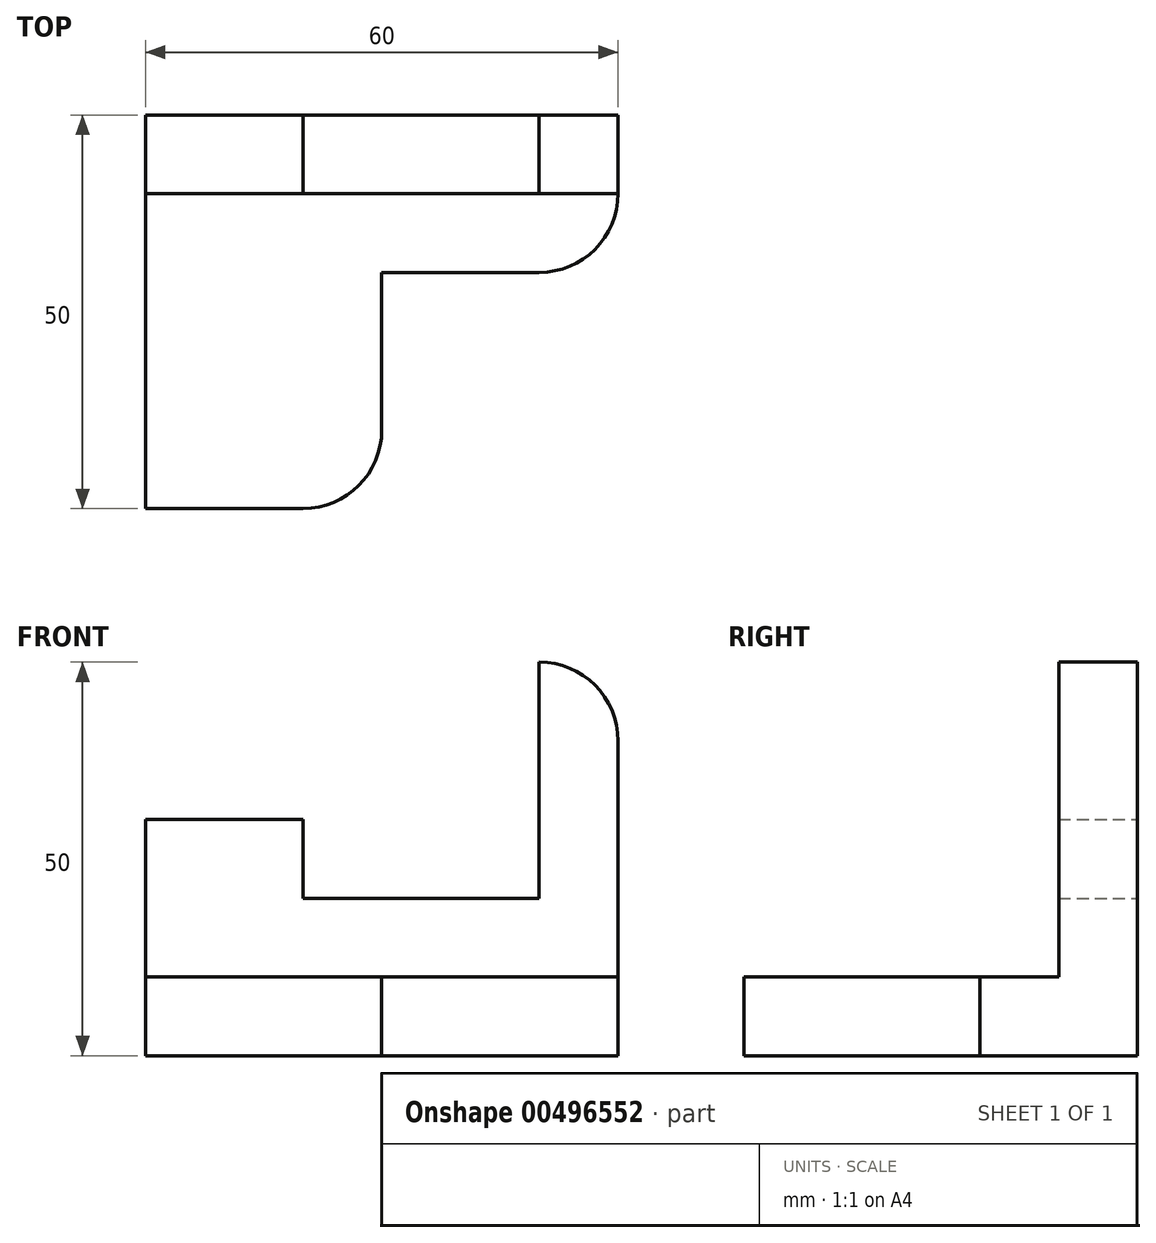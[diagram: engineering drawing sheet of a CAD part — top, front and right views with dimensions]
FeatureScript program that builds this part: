
annotation { "Feature Type Name" : "Feature", "Feature Type Description" : "" }
export const myFeature = defineFeature(function(context is Context, id is Id, definition is map)
    precondition{}
    {
        {
            var Q0;
            Q0=qCreatedBy(makeId("Top.planeOp"),FACE);
            var sketch = newSketch(context, id + "F0", { "sketchPlane" : qUnion([Q0])});
            skLineSegment(sketch, "E0", {"start": v(20, 0) * mm, "end": v(0, 0) * mm});
            skPoint(sketch, "E1.visualSharp", {"position": v(60, 30) * mm});
            skPoint(sketch, "E2.visualSharp", {"position": v(30, 0) * mm});
            skLineSegment(sketch, "E3", {"start": v(0, 0) * mm, "end": v(60, 0) * mm});
            skLineSegment(sketch, "E4", {"start": v(60, 0) * mm, "end": v(60, -10) * mm});
            skLineSegment(sketch, "E5", {"start": v(50, -20) * mm, "end": v(30, -20) * mm});
            skLineSegment(sketch, "E6", {"start": v(0, 0) * mm, "end": v(0, -50) * mm});
            skLineSegment(sketch, "E7", {"start": v(0, -50) * mm, "end": v(20, -50) * mm});
            skLineSegment(sketch, "E8", {"start": v(30, -40) * mm, "end": v(30, -20) * mm});
            skPoint(sketch, "E9.end.orphan", {"position": v(30, 30) * mm});
            skPoint(sketch, "E10.start.orphan", {"position": v(60, 50) * mm});
            skPoint(sketch, "E11.visualSharp", {"position": v(60, -20) * mm});
            skArc(sketch, "E11.filletArc", {"start": v(50, -20) * mm, "mid": v(57.07, -17.07) * mm, "end": v(60, -10) * mm});
            skPoint(sketch, "E12.visualSharp", {"position": v(30, -50) * mm});
            skArc(sketch, "E12.filletArc", {"start": v(20, -50) * mm, "mid": v(27.07, -47.07) * mm, "end": v(30, -40) * mm});
            skSolve(sketch);
        }
        {
            var Q0;
            Q0=makeQuery(id+"F0.imprint","IMPRINT",FACE,{"disambiguationData":[TD([[makeQuery(id+"F0.imprint","IMPRINT",EDGE,{"derivedFrom":sQuery(id+"F0.wireOp",EDGE,"GN2Li1Eq-WtNi-iwNF-XVSt-34LqWLU6xrt7")}),-1.0]])]});
            var Q1;
            {var subQ1=sQuery(id+"F0.wireOp",EDGE,"E4");Q1=makeQuery(id+"F0.imprint","IMPRINT",FACE,{"disambiguationData":[TD([[makeQuery(id+"F0.imprint","IMPRINT",EDGE,{"derivedFrom":subQ1}),-1.0]])]});}
            extrude(context, id + "F1", {"entities" : qUnion([Q0, Q1]), "depth" : 10 * mm});
        }
        {
            var Q0;
            Q0=qCreatedBy(makeId("Front.planeOp"),FACE);
            var sketch = newSketch(context, id + "F2", { "sketchPlane" : qUnion([Q0])});
            skLineSegment(sketch, "E13", {"start": v(0, 0) * mm, "end": v(0, 30) * mm});
            skLineSegment(sketch, "E14", {"start": v(0, 30) * mm, "end": v(20, 30) * mm});
            skLineSegment(sketch, "E15", {"start": v(20, 30) * mm, "end": v(20, 20) * mm});
            skLineSegment(sketch, "E16", {"start": v(20, 20) * mm, "end": v(50, 20) * mm});
            skLineSegment(sketch, "E17", {"start": v(50, 20) * mm, "end": v(50, 50) * mm});
            skLineSegment(sketch, "E18", {"start": v(50, 50) * mm, "end": v(50, 50) * mm});
            skLineSegment(sketch, "E19", {"start": v(60, 40) * mm, "end": v(60, 10) * mm});
            skLineSegment(sketch, "E20", {"start": v(60, 10) * mm, "end": v(0, 10) * mm});
            skPoint(sketch, "E21.visualSharp", {"position": v(60, 50) * mm});
            skArc(sketch, "E21.filletArc", {"start": v(60, 40) * mm, "mid": v(57.07, 47.07) * mm, "end": v(50, 50) * mm});
            skSolve(sketch);
        }
        {
            var Q0;
            Q0 = qSketchRegion(id + "F2", true);
            extrude(context, id + "F3", {"entities" : qUnion([Q0]), "operationType" : NewBodyOperationType.ADD, "depth" : 10 * mm});
        }
    });
